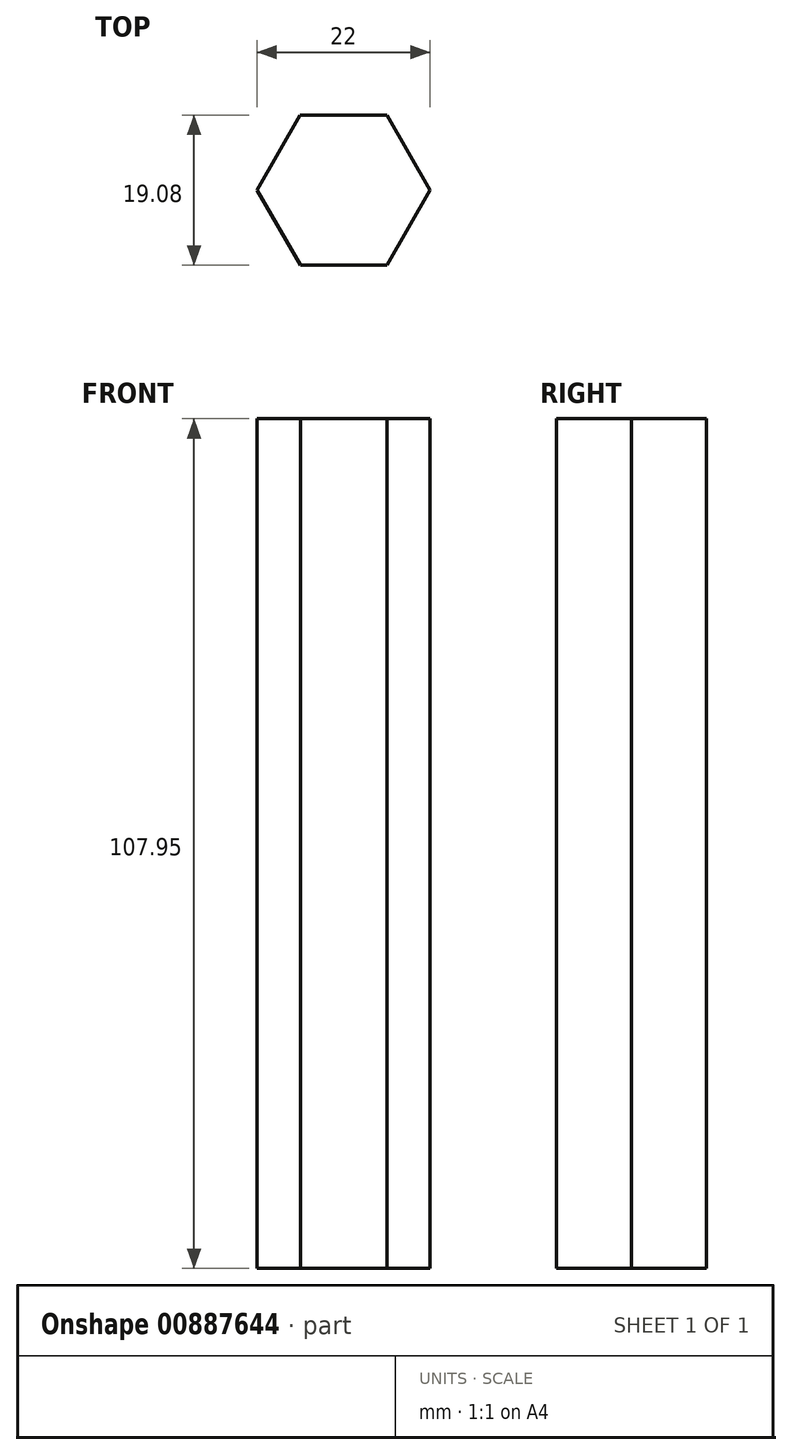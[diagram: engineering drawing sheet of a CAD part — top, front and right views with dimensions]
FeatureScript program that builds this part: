
annotation { "Feature Type Name" : "Feature", "Feature Type Description" : "" }
export const myFeature = defineFeature(function(context is Context, id is Id, definition is map)
    precondition{}
    {
        {
            var Q0;
            Q0=qCreatedBy(makeId("Top.planeOp"),FACE);
            var sketch = newSketch(context, id + "F0", { "sketchPlane" : qUnion([Q0])});
            skCircle(sketch, "E0.cCircle", {"center": v(0, 0) * mm, "radius": 9.53 * mm, "construction": true});
            skLineSegment(sketch, "E0.0", {"start": v(11, 0.02) * mm, "end": v(5.52, -9.51) * mm});
            skLineSegment(sketch, "E0.1", {"start": v(5.52, -9.51) * mm, "end": v(-5.48, -9.54) * mm});
            skLineSegment(sketch, "E0.2", {"start": v(-5.48, -9.54) * mm, "end": v(-11, -0.02) * mm});
            skLineSegment(sketch, "E0.3", {"start": v(-11, -0.02) * mm, "end": v(-5.52, 9.51) * mm});
            skLineSegment(sketch, "E0.4", {"start": v(-5.52, 9.51) * mm, "end": v(5.48, 9.54) * mm});
            skLineSegment(sketch, "E0.5", {"start": v(5.48, 9.54) * mm, "end": v(11, 0.02) * mm});
            skPoint(sketch, "E0.0.midPoint", {"position": v(8.26, -4.74) * mm});
            skSolve(sketch);
        }
        {
            var Q0;
            Q0=qCreatedBy(makeId("Right.planeOp"),FACE);
            var sketch = newSketch(context, id + "F1", { "sketchPlane" : qUnion([Q0])});
            skLineSegment(sketch, "E1", {"start": v(0, 0) * mm, "end": v(0, 107.95) * mm});
            skSolve(sketch);
        }
        {
            var Q0;
            Q0=makeQuery(id+"F0.imprint","IMPRINT",FACE,{"disambiguationData":[TD([[makeQuery(id+"F0.imprint","IMPRINT",EDGE,{"derivedFrom":sQuery(id+"F0.wireOp",EDGE,"E0.0")}),-1.0]])]});
            var Q1;
            Q1=sQuery(id+"F1.wireOp",EDGE,"E1");
            sweep(context, id + "F2", {"profiles" : qUnion([Q0]), "path" : qUnion([Q1])});
        }
    });
